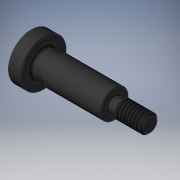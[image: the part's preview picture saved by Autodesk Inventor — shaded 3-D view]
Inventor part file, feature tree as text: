
AUTODESK INVENTOR PART (.ipt)
format: ipt  version: 2019 (Build 230136000, 136)  size: 173,568 bytes
history: native  units: mm
features: revolve x1, thread x1, extrude x1
ambient origin geometry x8: Origin, YZ Plane, XZ Plane, XY Plane, X Axis, Y Axis, Z Axis, Center Point
bodies: Solid1 (feature_tree)
feature tree (3):
  revolve  "Revolution1"  Angle=360.0deg
  thread  "Thread1"  [1 undecoded]
  extrude  "Extrusion1"  Depth=1.6mm TaperAngle=0.0deg
note: 1 required parameter value undecoded (feature->parameter linkage not recoverable at this tier; creation-order binding heuristic only, values carry confidence <= 0.55)
